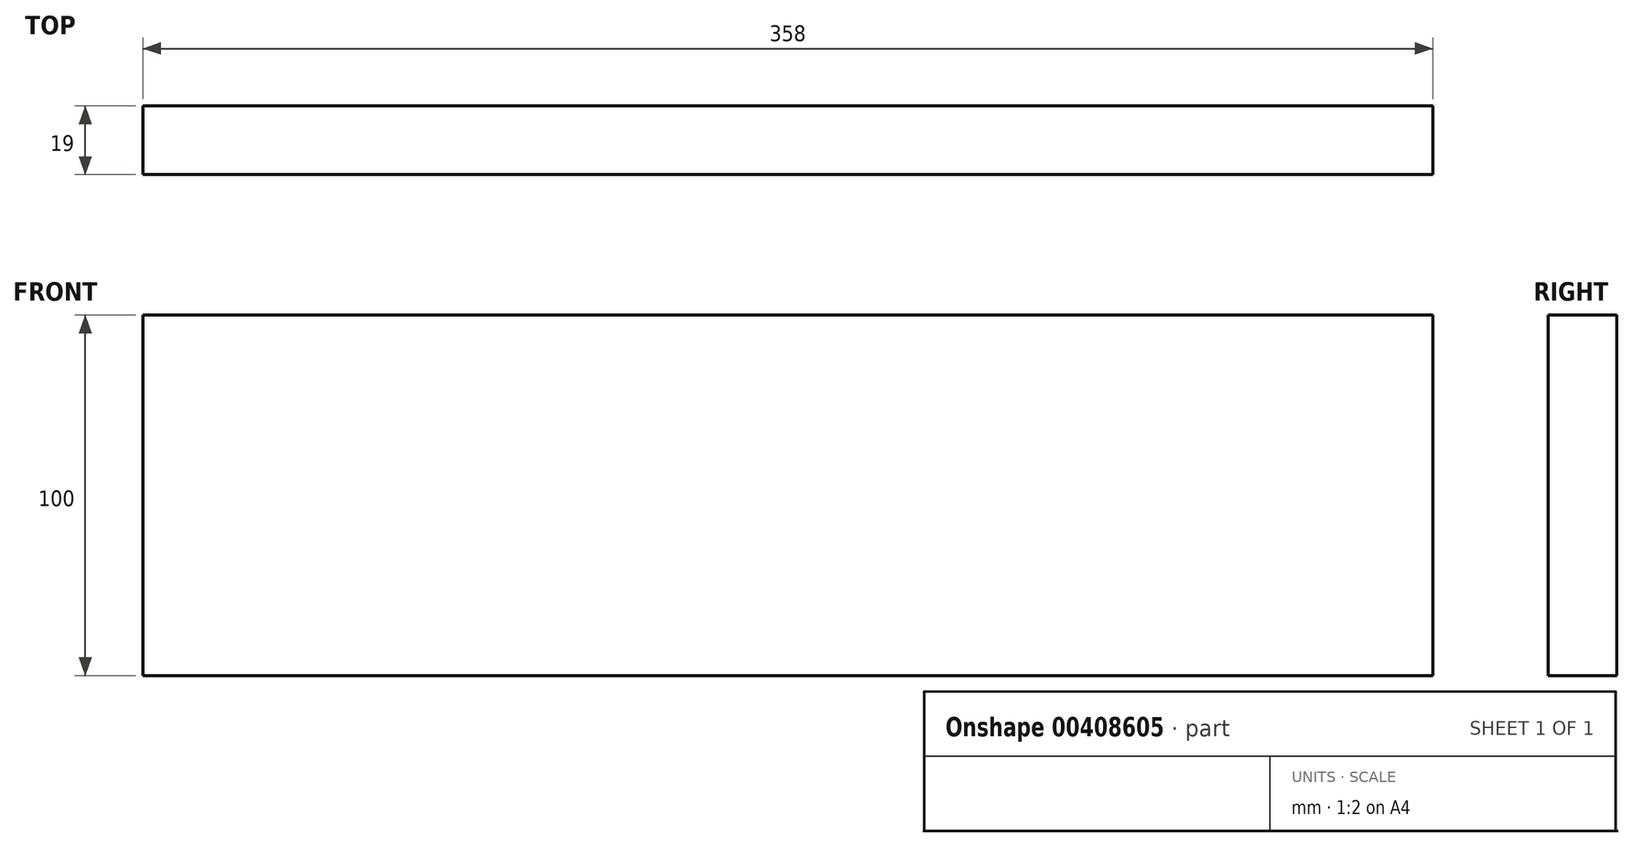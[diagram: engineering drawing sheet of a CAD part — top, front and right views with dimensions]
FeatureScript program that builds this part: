
annotation { "Feature Type Name" : "Feature", "Feature Type Description" : "" }
export const myFeature = defineFeature(function(context is Context, id is Id, definition is map)
    precondition{}
    {
        {
            var Q0;
            Q0=qCreatedBy(makeId("Front.planeOp"),FACE);
            var sketch = newSketch(context, id + "F0", { "sketchPlane" : qUnion([Q0])});
            skLineSegment(sketch, "E0.bottom", {"start": v(0, 100) * mm, "end": v(358, 100) * mm});
            skLineSegment(sketch, "E0.top", {"start": v(0, 0) * mm, "end": v(358, 0) * mm});
            skLineSegment(sketch, "E0.left", {"start": v(0, 100) * mm, "end": v(0, 0) * mm});
            skLineSegment(sketch, "E0.right", {"start": v(358, 100) * mm, "end": v(358, 0) * mm});
            skSolve(sketch);
        }
        {
            var Q0;
            Q0 = qSketchRegion(id + "F0", true);
            extrude(context, id + "F1", {"entities" : qUnion([Q0]), "depth" : 19 * mm});
        }
    });
